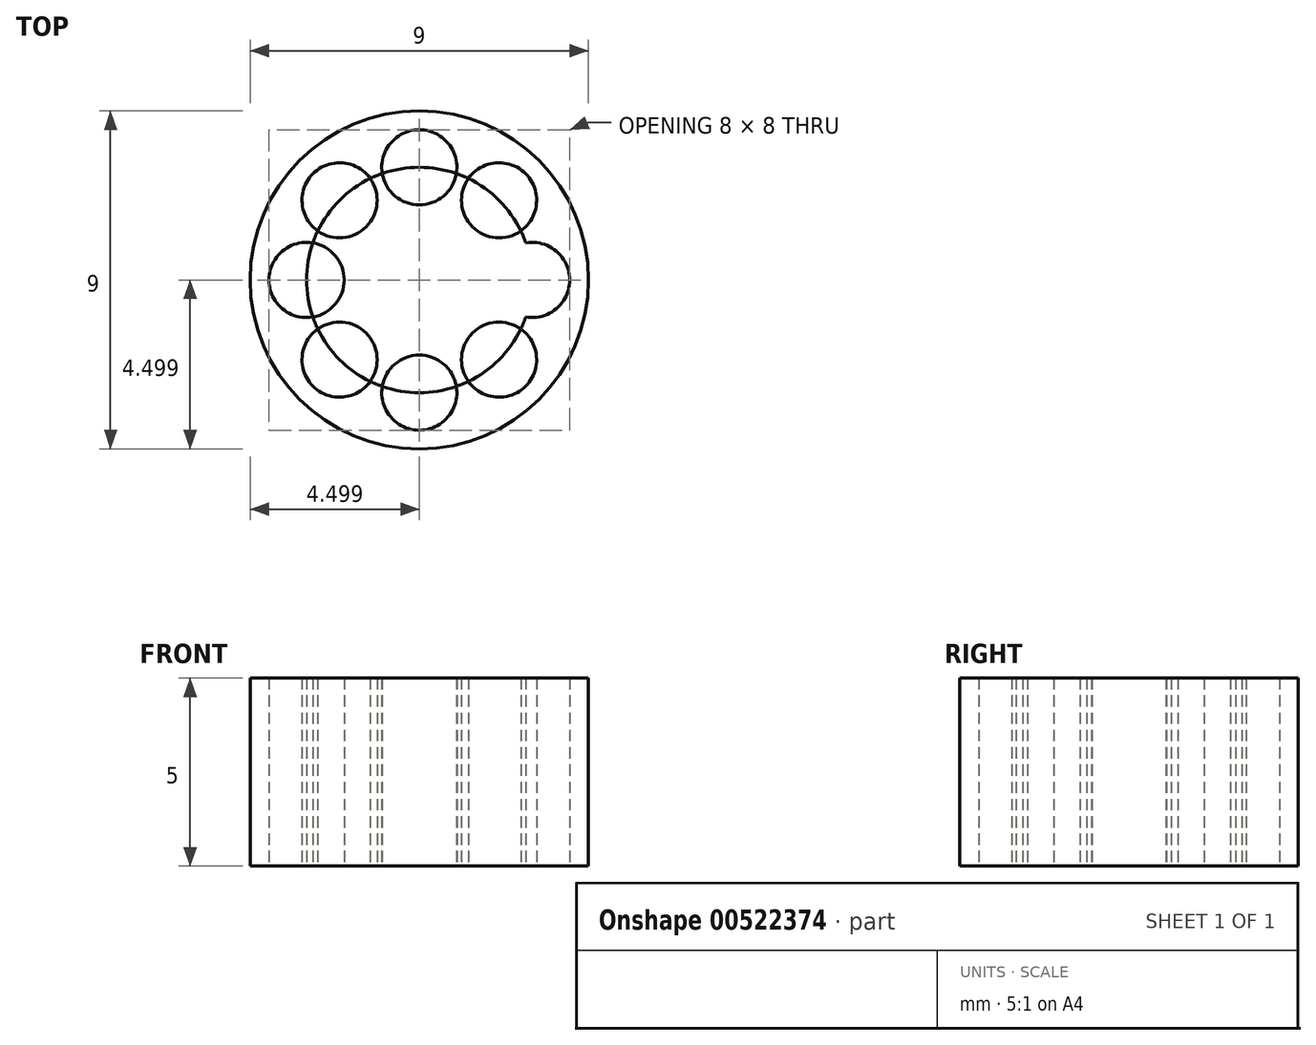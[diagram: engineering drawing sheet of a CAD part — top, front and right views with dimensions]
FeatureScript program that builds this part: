
annotation { "Feature Type Name" : "Feature", "Feature Type Description" : "" }
export const myFeature = defineFeature(function(context is Context, id is Id, definition is map)
    precondition{}
    {
        {
            var Q0;
            Q0=qCreatedBy(makeId("Top.planeOp"),FACE);
            var sketch = newSketch(context, id + "F0", { "sketchPlane" : qUnion([Q0])});
            skCircle(sketch, "E0", {"center": v(0.12, -0.08) * mm, "radius": 4.5 * mm});
            skCircle(sketch, "E1", {"center": v(0.12, -0.08) * mm, "radius": 3 * mm});
            skCircle(sketch, "E2", {"center": v(3.12, -0.08) * mm, "radius": 1 * mm});
            skCircle(sketch, "E3.1.0", {"center": v(2.24, 2.04) * mm, "radius": 1 * mm});
            skCircle(sketch, "E3.2.0", {"center": v(0.12, 2.92) * mm, "radius": 1 * mm});
            skCircle(sketch, "E3.3.0", {"center": v(-2, 2.04) * mm, "radius": 1 * mm});
            skCircle(sketch, "E3.4.0", {"center": v(-2.88, -0.08) * mm, "radius": 1 * mm});
            skCircle(sketch, "E3.5.0", {"center": v(-2, -2.2) * mm, "radius": 1 * mm});
            skCircle(sketch, "E3.6.0", {"center": v(0.12, -3.08) * mm, "radius": 1 * mm});
            skCircle(sketch, "E3.7.0", {"center": v(2.24, -2.2) * mm, "radius": 1 * mm});
            skSolve(sketch);
        }
        {
            var Q0;
            Q0=makeQuery(id+"F0.imprint","IMPRINT",FACE,{"disambiguationData":[TD([[makeQuery(id+"F0.imprint","IMPRINT",EDGE,{"derivedFrom":sQuery(id+"F0.wireOp",EDGE,"E0")}),1.0]])]});
            var Q1;
            {var subQ0=sQuery(id+"F0.wireOp",EDGE,"E1");var subQ1=makeQuery(id+"F0.imprint","IMPRINT",VERTEX,{"derivedFrom":subQ0});Q1=makeQuery(id+"F0.imprint","IMPRINT",FACE,{"disambiguationData":[TD([[makeQuery(id+"F0.imprint","IMPRINT",EDGE,{"disambiguationData":[TD([[subQ1,-1.0]])],"derivedFrom":subQ0}),1.0]])]});}
            var Q2;
            {var subQ0=sQuery(id+"F0.wireOp",EDGE,"E3.1.0");var subQ1=sQuery(id+"F0.wireOp",EDGE,"E1");var subQ2=makeQuery(id+"F0.imprint","INTERSECT",VERTEX,{"disambiguationData":[OD(0.0)],"derivedFrom":[subQ1,subQ0]});Q2=makeQuery(id+"F0.imprint","IMPRINT",FACE,{"disambiguationData":[TD([[makeQuery(id+"F0.imprint","IMPRINT",EDGE,{"disambiguationData":[TD([[subQ2,-1.0]])],"derivedFrom":subQ1}),1.0]])]});}
            var Q3;
            {var subQ0=sQuery(id+"F0.wireOp",EDGE,"E3.2.0");var subQ1=sQuery(id+"F0.wireOp",EDGE,"E1");var subQ2=makeQuery(id+"F0.imprint","INTERSECT",VERTEX,{"disambiguationData":[OD(0.0)],"derivedFrom":[subQ1,subQ0]});Q3=makeQuery(id+"F0.imprint","IMPRINT",FACE,{"disambiguationData":[TD([[makeQuery(id+"F0.imprint","IMPRINT",EDGE,{"disambiguationData":[TD([[subQ2,-1.0]])],"derivedFrom":subQ1}),1.0]])]});}
            var Q4;
            {var subQ0=sQuery(id+"F0.wireOp",EDGE,"E3.3.0");var subQ1=sQuery(id+"F0.wireOp",EDGE,"E1");var subQ2=makeQuery(id+"F0.imprint","INTERSECT",VERTEX,{"disambiguationData":[OD(0.0)],"derivedFrom":[subQ1,subQ0]});Q4=makeQuery(id+"F0.imprint","IMPRINT",FACE,{"disambiguationData":[TD([[makeQuery(id+"F0.imprint","IMPRINT",EDGE,{"disambiguationData":[TD([[subQ2,-1.0]])],"derivedFrom":subQ1}),1.0]])]});}
            var Q5;
            {var subQ0=sQuery(id+"F0.wireOp",EDGE,"E3.4.0");var subQ1=sQuery(id+"F0.wireOp",EDGE,"E1");var subQ2=makeQuery(id+"F0.imprint","INTERSECT",VERTEX,{"disambiguationData":[OD(0.0)],"derivedFrom":[subQ1,subQ0]});Q5=makeQuery(id+"F0.imprint","IMPRINT",FACE,{"disambiguationData":[TD([[makeQuery(id+"F0.imprint","IMPRINT",EDGE,{"disambiguationData":[TD([[subQ2,-1.0]])],"derivedFrom":subQ1}),1.0]])]});}
            var Q6;
            {var subQ0=sQuery(id+"F0.wireOp",EDGE,"E3.5.0");var subQ1=sQuery(id+"F0.wireOp",EDGE,"E1");var subQ2=makeQuery(id+"F0.imprint","INTERSECT",VERTEX,{"disambiguationData":[OD(0.0)],"derivedFrom":[subQ1,subQ0]});Q6=makeQuery(id+"F0.imprint","IMPRINT",FACE,{"disambiguationData":[TD([[makeQuery(id+"F0.imprint","IMPRINT",EDGE,{"disambiguationData":[TD([[subQ2,-1.0]])],"derivedFrom":subQ1}),1.0]])]});}
            var Q7;
            {var subQ0=sQuery(id+"F0.wireOp",EDGE,"E3.6.0");var subQ1=sQuery(id+"F0.wireOp",EDGE,"E1");var subQ2=makeQuery(id+"F0.imprint","INTERSECT",VERTEX,{"disambiguationData":[OD(0.0)],"derivedFrom":[subQ1,subQ0]});Q7=makeQuery(id+"F0.imprint","IMPRINT",FACE,{"disambiguationData":[TD([[makeQuery(id+"F0.imprint","IMPRINT",EDGE,{"disambiguationData":[TD([[subQ2,-1.0]])],"derivedFrom":subQ1}),1.0]])]});}
            var Q8;
            {var subQ0=sQuery(id+"F0.wireOp",EDGE,"E3.7.0");var subQ1=sQuery(id+"F0.wireOp",EDGE,"E1");var subQ2=makeQuery(id+"F0.imprint","INTERSECT",VERTEX,{"disambiguationData":[OD(0.0)],"derivedFrom":[subQ1,subQ0]});Q8=makeQuery(id+"F0.imprint","IMPRINT",FACE,{"disambiguationData":[TD([[makeQuery(id+"F0.imprint","IMPRINT",EDGE,{"disambiguationData":[TD([[subQ2,-1.0]])],"derivedFrom":subQ1}),1.0]])]});}
            var Q9;
            {var subQ0=sQuery(id+"F0.wireOp",EDGE,"E1");var subQ1=makeQuery(id+"F0.imprint","IMPRINT",VERTEX,{"derivedFrom":subQ0});Q9=makeQuery(id+"F0.imprint","IMPRINT",FACE,{"disambiguationData":[TD([[makeQuery(id+"F0.imprint","IMPRINT",EDGE,{"disambiguationData":[TD([[subQ1,-1.0]])],"derivedFrom":subQ0}),-1.0]])]});}
            var Q10;
            {var subQ0=sQuery(id+"F0.wireOp",EDGE,"E3.1.0");var subQ4=makeQuery(id+"F0.imprint","IMPRINT",VERTEX,{"derivedFrom":subQ0});Q10=makeQuery(id+"F0.imprint","IMPRINT",FACE,{"disambiguationData":[TD([[makeQuery(id+"F0.imprint","IMPRINT",EDGE,{"disambiguationData":[TD([[subQ4,-1.0]])],"derivedFrom":subQ0}),1.0]])]});}
            var Q11;
            {var subQ0=sQuery(id+"F0.wireOp",EDGE,"E3.2.0");var subQ4=makeQuery(id+"F0.imprint","IMPRINT",VERTEX,{"derivedFrom":subQ0});Q11=makeQuery(id+"F0.imprint","IMPRINT",FACE,{"disambiguationData":[TD([[makeQuery(id+"F0.imprint","IMPRINT",EDGE,{"disambiguationData":[TD([[subQ4,-1.0]])],"derivedFrom":subQ0}),1.0]])]});}
            var Q12;
            {var subQ0=sQuery(id+"F0.wireOp",EDGE,"E3.3.0");var subQ4=makeQuery(id+"F0.imprint","IMPRINT",VERTEX,{"derivedFrom":subQ0});Q12=makeQuery(id+"F0.imprint","IMPRINT",FACE,{"disambiguationData":[TD([[makeQuery(id+"F0.imprint","IMPRINT",EDGE,{"disambiguationData":[TD([[subQ4,1.0]])],"derivedFrom":subQ0}),1.0]])]});}
            var Q13;
            {var subQ0=sQuery(id+"F0.wireOp",EDGE,"E3.4.0");var subQ4=makeQuery(id+"F0.imprint","IMPRINT",VERTEX,{"derivedFrom":subQ0});Q13=makeQuery(id+"F0.imprint","IMPRINT",FACE,{"disambiguationData":[TD([[makeQuery(id+"F0.imprint","IMPRINT",EDGE,{"disambiguationData":[TD([[subQ4,1.0]])],"derivedFrom":subQ0}),1.0]])]});}
            var Q14;
            {var subQ0=sQuery(id+"F0.wireOp",EDGE,"E3.5.0");var subQ4=makeQuery(id+"F0.imprint","IMPRINT",VERTEX,{"derivedFrom":subQ0});Q14=makeQuery(id+"F0.imprint","IMPRINT",FACE,{"disambiguationData":[TD([[makeQuery(id+"F0.imprint","IMPRINT",EDGE,{"disambiguationData":[TD([[subQ4,1.0]])],"derivedFrom":subQ0}),1.0]])]});}
            var Q15;
            {var subQ0=sQuery(id+"F0.wireOp",EDGE,"E3.6.0");var subQ4=makeQuery(id+"F0.imprint","IMPRINT",VERTEX,{"derivedFrom":subQ0});Q15=makeQuery(id+"F0.imprint","IMPRINT",FACE,{"disambiguationData":[TD([[makeQuery(id+"F0.imprint","IMPRINT",EDGE,{"disambiguationData":[TD([[subQ4,1.0]])],"derivedFrom":subQ0}),1.0]])]});}
            var Q16;
            {var subQ0=sQuery(id+"F0.wireOp",EDGE,"E3.7.0");var subQ4=makeQuery(id+"F0.imprint","IMPRINT",VERTEX,{"derivedFrom":subQ0});Q16=makeQuery(id+"F0.imprint","IMPRINT",FACE,{"disambiguationData":[TD([[makeQuery(id+"F0.imprint","IMPRINT",EDGE,{"disambiguationData":[TD([[subQ4,1.0]])],"derivedFrom":subQ0}),1.0]])]});}
            extrude(context, id + "F1", {"entities" : qUnion([Q0, Q1, Q2, Q3, Q4, Q5, Q6, Q7, Q8, Q9, Q10, Q11, Q12, Q13, Q14, Q15, Q16]), "depth" : 5 * mm, "offsetDistance" : 25 * mm});
        }
    });
